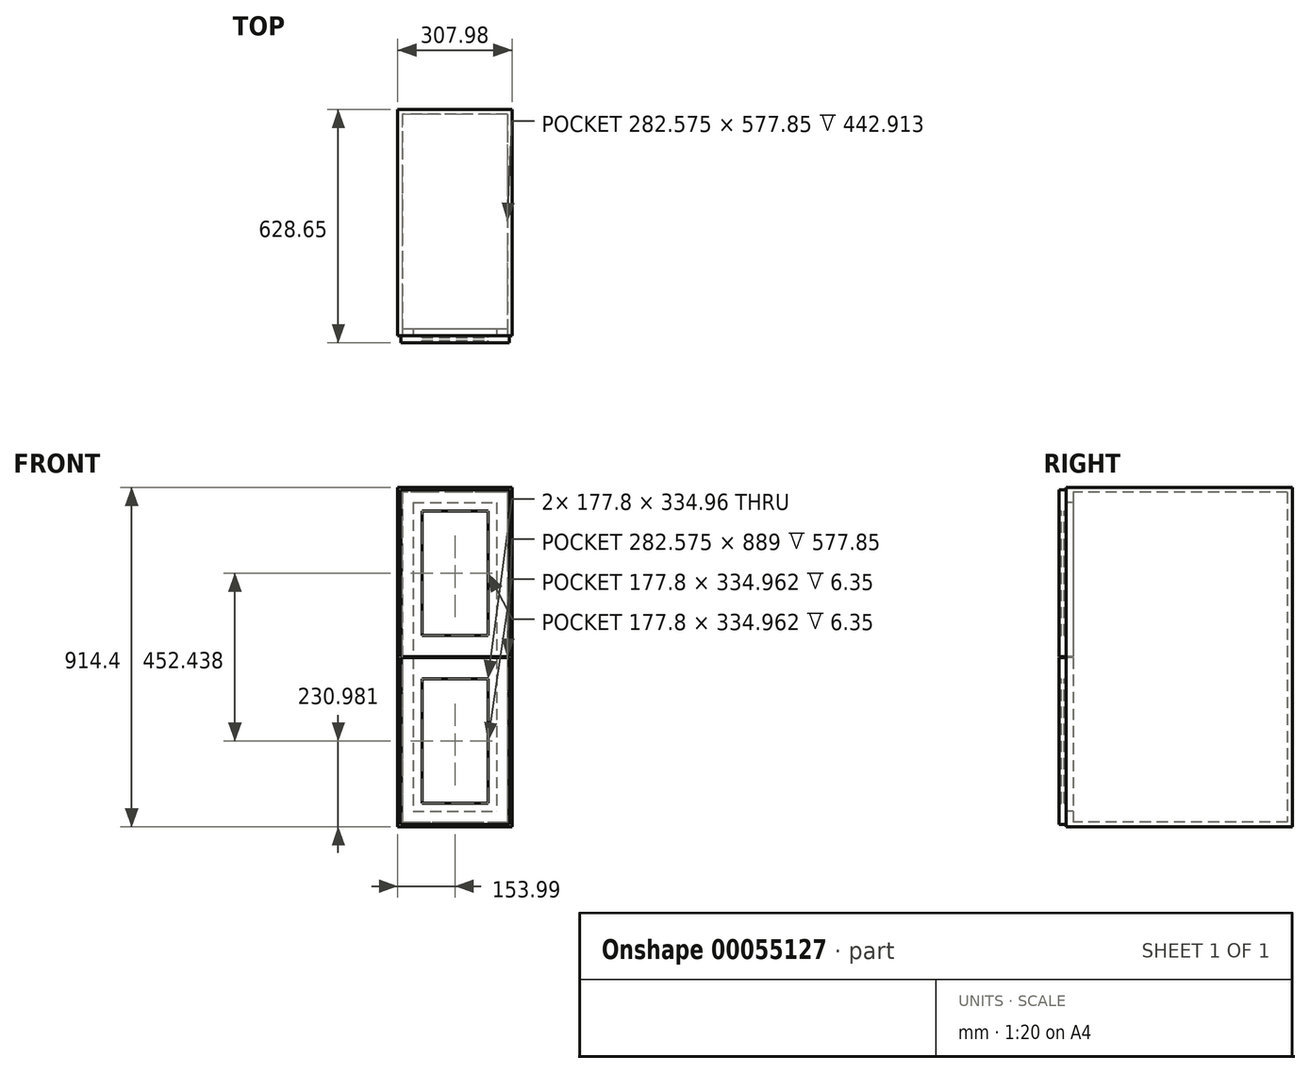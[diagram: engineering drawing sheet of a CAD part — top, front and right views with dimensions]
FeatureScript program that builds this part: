
annotation { "Feature Type Name" : "Feature", "Feature Type Description" : "" }
export const myFeature = defineFeature(function(context is Context, id is Id, definition is map)
    precondition{}
    {
        {
            var Q0;
            Q0=qCreatedBy(makeId("Top.planeOp"),FACE);
            var sketch = newSketch(context, id + "F0", { "sketchPlane" : qUnion([Q0])});
            skLineSegment(sketch, "E0.rect.bottom", {"start": v(153.99, 304.8) * mm, "end": v(-153.99, 304.8) * mm});
            skLineSegment(sketch, "E0.rect.top", {"start": v(153.99, -304.8) * mm, "end": v(-153.99, -304.8) * mm});
            skLineSegment(sketch, "E0.rect.left", {"start": v(153.99, 304.8) * mm, "end": v(153.99, -304.8) * mm});
            skLineSegment(sketch, "E0.rect.right", {"start": v(-153.99, 304.8) * mm, "end": v(-153.99, -304.8) * mm});
            skPoint(sketch, "E0.rect.middle", {"position": v(0, 0) * mm});
            skSolve(sketch);
        }
        {
            var Q0;
            Q0=qSketchRegion(id+"F0",true);
            extrude(context, id + "F1", {"entities" : qUnion([Q0]), "depth" : 914.4 * mm});
        }
        {
            var Q0;
            Q0=makeQuery(id+"F1.opExtrude","SWEPT_FACE",FACE,{"disambiguationData":[OSD([sQuery(id+"F0.wireOp",EDGE,"E0.rect.top")])]});
            shell(context, id + "F2", {"entities" : qUnion([Q0]), "thickness" : 12.7 * mm});
        }
        {
            var Q0;
            Q0=makeQuery(id+"F1.opExtrude","SWEPT_FACE",FACE,{"disambiguationData":[OSD([sQuery(id+"F0.wireOp",EDGE,"E0.rect.top")])]});
            var sketch = newSketch(context, id + "F3", { "sketchPlane" : qUnion([Q0])});
            skLineSegment(sketch, "E1", {"start": v(-153.99, 457.2) * mm, "end": v(153.99, 457.2) * mm, "construction": true});
            skLineSegment(sketch, "E2.rect.bottom", {"start": v(-153.99, 436.56) * mm, "end": v(153.99, 436.56) * mm});
            skLineSegment(sketch, "E2.rect.top", {"start": v(-153.99, 477.84) * mm, "end": v(153.99, 477.84) * mm});
            skLineSegment(sketch, "E2.rect.left", {"start": v(-153.99, 436.56) * mm, "end": v(-153.99, 477.84) * mm});
            skLineSegment(sketch, "E2.rect.right", {"start": v(153.99, 436.56) * mm, "end": v(153.99, 477.84) * mm});
            skPoint(sketch, "E2.rect.middle", {"position": v(0, 457.2) * mm});
            skLineSegment(sketch, "E3.bottom", {"start": v(-146.05, 6.35) * mm, "end": v(146.05, 6.35) * mm});
            skLineSegment(sketch, "E3.top", {"start": v(-146.05, 455.61) * mm, "end": v(146.05, 455.61) * mm});
            skLineSegment(sketch, "E3.left", {"start": v(-146.05, 6.35) * mm, "end": v(-146.05, 455.61) * mm});
            skLineSegment(sketch, "E3.right", {"start": v(146.05, 6.35) * mm, "end": v(146.05, 455.61) * mm});
            skLineSegment(sketch, "E4.rect.bottom", {"start": v(-112.71, 873.13) * mm, "end": v(112.71, 873.13) * mm});
            skLineSegment(sketch, "E4.rect.top", {"start": v(-112.71, 41.28) * mm, "end": v(112.71, 41.28) * mm});
            skLineSegment(sketch, "E4.rect.left", {"start": v(-112.71, 873.13) * mm, "end": v(-112.71, 41.28) * mm});
            skLineSegment(sketch, "E4.rect.right", {"start": v(112.71, 873.13) * mm, "end": v(112.71, 41.28) * mm});
            skLineSegment(sketch, "E5.bottom", {"start": v(-88.9, 63.5) * mm, "end": v(88.9, 63.5) * mm});
            skLineSegment(sketch, "E5.top", {"start": v(-88.9, 398.46) * mm, "end": v(88.9, 398.46) * mm});
            skLineSegment(sketch, "E5.left", {"start": v(-88.9, 63.5) * mm, "end": v(-88.9, 398.46) * mm});
            skLineSegment(sketch, "E5.right", {"start": v(88.9, 63.5) * mm, "end": v(88.9, 398.46) * mm});
            skLineSegment(sketch, "E6.bottom", {"start": v(-146.05, 458.79) * mm, "end": v(146.05, 458.79) * mm});
            skLineSegment(sketch, "E6.top", {"start": v(-146.05, 908.05) * mm, "end": v(146.05, 908.05) * mm});
            skLineSegment(sketch, "E6.left", {"start": v(-146.05, 458.79) * mm, "end": v(-146.05, 908.05) * mm});
            skLineSegment(sketch, "E6.right", {"start": v(146.05, 458.79) * mm, "end": v(146.05, 908.05) * mm});
            skLineSegment(sketch, "E7.bottom", {"start": v(-88.9, 515.94) * mm, "end": v(88.9, 515.94) * mm});
            skLineSegment(sketch, "E7.top", {"start": v(-88.9, 850.9) * mm, "end": v(88.9, 850.9) * mm});
            skLineSegment(sketch, "E7.left", {"start": v(-88.9, 515.94) * mm, "end": v(-88.9, 850.9) * mm});
            skLineSegment(sketch, "E7.right", {"start": v(88.9, 515.94) * mm, "end": v(88.9, 850.9) * mm});
            skSolve(sketch);
        }
        {
            var Q0;
            {var subQ1=sQuery(id+"F3.wireOp",EDGE,"E4.rect.bottom");Q0=makeQuery(id+"F3.imprint","IMPRINT",FACE,{"disambiguationData":[TD([[makeQuery(id+"F3.imprint","IMPRINT",EDGE,{"derivedFrom":subQ1}),1.0]])]});}
            var Q1;
            {var subQ0=sQuery(id+"F0.wireOp",EDGE,"E0.rect.top");var subQ1=makeQuery(id+"F1.opExtrude","CAP_EDGE",EDGE,{"disambiguationData":[OSD([subQ0])],"isStart":false});Q1=makeQuery(id+"F3.imprint","IMPRINT",FACE,{"disambiguationData":[TD([[makeQuery(id+"F3.imprint","IMPRINT",EDGE,{"derivedFrom":subQ1}),1.0]])]});}
            var Q2;
            {var subQ0=sQuery(id+"F3.wireOp",EDGE,"E4.rect.top");Q2=makeQuery(id+"F3.imprint","IMPRINT",FACE,{"disambiguationData":[TD([[makeQuery(id+"F3.imprint","IMPRINT",EDGE,{"derivedFrom":subQ0}),-1.0]])]});}
            var Q3;
            {var subQ1=sQuery(id+"F3.wireOp",EDGE,"E3.bottom");Q3=makeQuery(id+"F3.imprint","IMPRINT",FACE,{"disambiguationData":[TD([[makeQuery(id+"F3.imprint","IMPRINT",EDGE,{"derivedFrom":subQ1}),-1.0]])]});}
            var Q4;
            {var subQ0=sQuery(id+"F3.wireOp",EDGE,"E3.bottom");Q4=makeQuery(id+"F3.imprint","IMPRINT",FACE,{"disambiguationData":[TD([[makeQuery(id+"F3.imprint","IMPRINT",EDGE,{"derivedFrom":subQ0}),1.0]])]});}
            var Q5;
            {var subQ0=sQuery(id+"F3.wireOp",EDGE,"E4.rect.left");var subQ1=sQuery(id+"F3.wireOp",EDGE,"E2.rect.bottom");var subQ2=makeQuery(id+"F3.imprint","INTERSECT",VERTEX,{"derivedFrom":[subQ1,subQ0]});Q5=makeQuery(id+"F3.imprint","IMPRINT",FACE,{"disambiguationData":[TD([[makeQuery(id+"F3.imprint","IMPRINT",EDGE,{"disambiguationData":[TD([[subQ2,1.0]])],"derivedFrom":subQ0}),-1.0]])]});}
            var Q6;
            {var subQ0=sQuery(id+"F3.wireOp",EDGE,"E2.rect.left");Q6=makeQuery(id+"F3.imprint","IMPRINT",FACE,{"disambiguationData":[TD([[makeQuery(id+"F3.imprint","IMPRINT",EDGE,{"derivedFrom":subQ0}),1.0]])]});}
            var Q7;
            {var subQ0=sQuery(id+"F3.wireOp",EDGE,"E3.left");var subQ5=sQuery(id+"F3.wireOp",EDGE,"E3.top");var subQ6=makeQuery(id+"F3.imprint","INTERSECT",VERTEX,{"derivedFrom":[subQ5,subQ0]});Q7=makeQuery(id+"F3.imprint","IMPRINT",FACE,{"disambiguationData":[TD([[makeQuery(id+"F3.imprint","IMPRINT",EDGE,{"disambiguationData":[TD([[subQ6,1.0]])],"derivedFrom":subQ0}),-1.0]])]});}
            var Q8;
            {var subQ0=sQuery(id+"F3.wireOp",EDGE,"E4.rect.left");var subQ1=sQuery(id+"F3.wireOp",EDGE,"E2.rect.top");var subQ2=makeQuery(id+"F3.imprint","INTERSECT",VERTEX,{"derivedFrom":[subQ1,subQ0]});Q8=makeQuery(id+"F3.imprint","IMPRINT",FACE,{"disambiguationData":[TD([[makeQuery(id+"F3.imprint","IMPRINT",EDGE,{"disambiguationData":[TD([[subQ2,-1.0]])],"derivedFrom":subQ0}),-1.0]])]});}
            var Q9;
            {var subQ0=sQuery(id+"F3.wireOp",EDGE,"E4.rect.right");var subQ1=sQuery(id+"F3.wireOp",EDGE,"E2.rect.top");var subQ2=makeQuery(id+"F3.imprint","INTERSECT",VERTEX,{"derivedFrom":[subQ1,subQ0]});Q9=makeQuery(id+"F3.imprint","IMPRINT",FACE,{"disambiguationData":[TD([[makeQuery(id+"F3.imprint","IMPRINT",EDGE,{"disambiguationData":[TD([[subQ2,-1.0]])],"derivedFrom":subQ0}),1.0]])]});}
            var Q10;
            {var subQ0=sQuery(id+"F3.wireOp",EDGE,"E4.rect.right");var subQ1=sQuery(id+"F3.wireOp",EDGE,"E2.rect.bottom");var subQ2=makeQuery(id+"F3.imprint","INTERSECT",VERTEX,{"derivedFrom":[subQ1,subQ0]});Q10=makeQuery(id+"F3.imprint","IMPRINT",FACE,{"disambiguationData":[TD([[makeQuery(id+"F3.imprint","IMPRINT",EDGE,{"disambiguationData":[TD([[subQ2,1.0]])],"derivedFrom":subQ0}),1.0]])]});}
            var Q11;
            {var subQ7=sQuery(id+"F3.wireOp",EDGE,"E2.rect.right");Q11=makeQuery(id+"F3.imprint","IMPRINT",FACE,{"disambiguationData":[TD([[makeQuery(id+"F3.imprint","IMPRINT",EDGE,{"derivedFrom":subQ7}),-1.0]])]});}
            var Q12;
            {var subQ0=sQuery(id+"F3.wireOp",EDGE,"E3.right");var subQ5=sQuery(id+"F3.wireOp",EDGE,"E3.top");var subQ6=makeQuery(id+"F3.imprint","INTERSECT",VERTEX,{"derivedFrom":[subQ5,subQ0]});Q12=makeQuery(id+"F3.imprint","IMPRINT",FACE,{"disambiguationData":[TD([[makeQuery(id+"F3.imprint","IMPRINT",EDGE,{"disambiguationData":[TD([[subQ6,1.0]])],"derivedFrom":subQ0}),1.0]])]});}
            extrude(context, id + "F4", {"entities" : qUnion([Q0, Q1, Q2, Q3, Q4, Q5, Q6, Q7, Q8, Q9, Q10, Q11, Q12]), "operationType" : NewBodyOperationType.ADD, "oppositeDirection" : true, "depth" : 19.05 * mm});
        }
        {
            var Q0;
            {var subQ0=sQuery(id+"F3.wireOp",EDGE,"E4.rect.top");Q0=makeQuery(id+"F3.imprint","IMPRINT",FACE,{"disambiguationData":[TD([[makeQuery(id+"F3.imprint","IMPRINT",EDGE,{"derivedFrom":subQ0}),-1.0]])]});}
            var Q1;
            {var subQ0=sQuery(id+"F3.wireOp",EDGE,"E3.bottom");Q1=makeQuery(id+"F3.imprint","IMPRINT",FACE,{"disambiguationData":[TD([[makeQuery(id+"F3.imprint","IMPRINT",EDGE,{"derivedFrom":subQ0}),1.0]])]});}
            var Q2;
            {var subQ1=sQuery(id+"F3.wireOp",EDGE,"E4.rect.top");Q2=makeQuery(id+"F3.imprint","IMPRINT",FACE,{"disambiguationData":[TD([[makeQuery(id+"F3.imprint","IMPRINT",EDGE,{"derivedFrom":subQ1}),1.0]])]});}
            var Q3;
            {var subQ0=sQuery(id+"F3.wireOp",EDGE,"E4.rect.left");var subQ1=sQuery(id+"F3.wireOp",EDGE,"E2.rect.bottom");var subQ2=makeQuery(id+"F3.imprint","INTERSECT",VERTEX,{"derivedFrom":[subQ1,subQ0]});Q3=makeQuery(id+"F3.imprint","IMPRINT",FACE,{"disambiguationData":[TD([[makeQuery(id+"F3.imprint","IMPRINT",EDGE,{"disambiguationData":[TD([[subQ2,-1.0]])],"derivedFrom":subQ1}),1.0]])]});}
            var Q4;
            {var subQ0=sQuery(id+"F3.wireOp",EDGE,"E4.rect.left");var subQ1=sQuery(id+"F3.wireOp",EDGE,"E2.rect.bottom");var subQ2=makeQuery(id+"F3.imprint","INTERSECT",VERTEX,{"derivedFrom":[subQ1,subQ0]});Q4=makeQuery(id+"F3.imprint","IMPRINT",FACE,{"disambiguationData":[TD([[makeQuery(id+"F3.imprint","IMPRINT",EDGE,{"disambiguationData":[TD([[subQ2,1.0]])],"derivedFrom":subQ0}),-1.0]])]});}
            var Q5;
            {var subQ0=sQuery(id+"F3.wireOp",EDGE,"E4.rect.right");var subQ1=sQuery(id+"F3.wireOp",EDGE,"E2.rect.bottom");var subQ2=makeQuery(id+"F3.imprint","INTERSECT",VERTEX,{"derivedFrom":[subQ1,subQ0]});Q5=makeQuery(id+"F3.imprint","IMPRINT",FACE,{"disambiguationData":[TD([[makeQuery(id+"F3.imprint","IMPRINT",EDGE,{"disambiguationData":[TD([[subQ2,1.0]])],"derivedFrom":subQ0}),1.0]])]});}
            var Q6;
            {var subQ0=sQuery(id+"F3.wireOp",EDGE,"E3.right");var subQ5=sQuery(id+"F3.wireOp",EDGE,"E3.top");var subQ6=makeQuery(id+"F3.imprint","INTERSECT",VERTEX,{"derivedFrom":[subQ5,subQ0]});Q6=makeQuery(id+"F3.imprint","IMPRINT",FACE,{"disambiguationData":[TD([[makeQuery(id+"F3.imprint","IMPRINT",EDGE,{"disambiguationData":[TD([[subQ6,1.0]])],"derivedFrom":subQ0}),1.0]])]});}
            var Q7;
            {var subQ0=sQuery(id+"F3.wireOp",EDGE,"E3.left");var subQ5=sQuery(id+"F3.wireOp",EDGE,"E3.top");var subQ6=makeQuery(id+"F3.imprint","INTERSECT",VERTEX,{"derivedFrom":[subQ5,subQ0]});Q7=makeQuery(id+"F3.imprint","IMPRINT",FACE,{"disambiguationData":[TD([[makeQuery(id+"F3.imprint","IMPRINT",EDGE,{"disambiguationData":[TD([[subQ6,1.0]])],"derivedFrom":subQ0}),-1.0]])]});}
            var Q8;
            {var subQ0=sQuery(id+"F3.wireOp",EDGE,"E4.rect.bottom");Q8=makeQuery(id+"F3.imprint","IMPRINT",FACE,{"disambiguationData":[TD([[makeQuery(id+"F3.imprint","IMPRINT",EDGE,{"derivedFrom":subQ0}),1.0]])]});}
            var Q9;
            {var subQ1=sQuery(id+"F3.wireOp",EDGE,"E4.rect.bottom");Q9=makeQuery(id+"F3.imprint","IMPRINT",FACE,{"disambiguationData":[TD([[makeQuery(id+"F3.imprint","IMPRINT",EDGE,{"derivedFrom":subQ1}),-1.0]])]});}
            var Q10;
            {var subQ0=sQuery(id+"F3.wireOp",EDGE,"E4.rect.left");var subQ1=sQuery(id+"F3.wireOp",EDGE,"E2.rect.top");var subQ2=makeQuery(id+"F3.imprint","INTERSECT",VERTEX,{"derivedFrom":[subQ1,subQ0]});Q10=makeQuery(id+"F3.imprint","IMPRINT",FACE,{"disambiguationData":[TD([[makeQuery(id+"F3.imprint","IMPRINT",EDGE,{"disambiguationData":[TD([[subQ2,-1.0]])],"derivedFrom":subQ0}),-1.0]])]});}
            var Q11;
            {var subQ0=sQuery(id+"F3.wireOp",EDGE,"E4.rect.left");var subQ1=sQuery(id+"F3.wireOp",EDGE,"E2.rect.top");var subQ2=makeQuery(id+"F3.imprint","INTERSECT",VERTEX,{"derivedFrom":[subQ1,subQ0]});Q11=makeQuery(id+"F3.imprint","IMPRINT",FACE,{"disambiguationData":[TD([[makeQuery(id+"F3.imprint","IMPRINT",EDGE,{"disambiguationData":[TD([[subQ2,-1.0]])],"derivedFrom":subQ1}),-1.0]])]});}
            var Q12;
            {var subQ0=sQuery(id+"F3.wireOp",EDGE,"E4.rect.right");var subQ1=sQuery(id+"F3.wireOp",EDGE,"E2.rect.top");var subQ2=makeQuery(id+"F3.imprint","INTERSECT",VERTEX,{"derivedFrom":[subQ1,subQ0]});Q12=makeQuery(id+"F3.imprint","IMPRINT",FACE,{"disambiguationData":[TD([[makeQuery(id+"F3.imprint","IMPRINT",EDGE,{"disambiguationData":[TD([[subQ2,-1.0]])],"derivedFrom":subQ0}),1.0]])]});}
            var Q13;
            {var subQ0=sQuery(id+"F3.wireOp",EDGE,"E6.right");var subQ5=sQuery(id+"F3.wireOp",EDGE,"E6.bottom");var subQ6=makeQuery(id+"F3.imprint","INTERSECT",VERTEX,{"derivedFrom":[subQ5,subQ0]});Q13=makeQuery(id+"F3.imprint","IMPRINT",FACE,{"disambiguationData":[TD([[makeQuery(id+"F3.imprint","IMPRINT",EDGE,{"disambiguationData":[TD([[subQ6,-1.0]])],"derivedFrom":subQ0}),1.0]])]});}
            var Q14;
            {var subQ1=sQuery(id+"F3.wireOp",EDGE,"E6.top");Q14=makeQuery(id+"F3.imprint","IMPRINT",FACE,{"disambiguationData":[TD([[makeQuery(id+"F3.imprint","IMPRINT",EDGE,{"derivedFrom":subQ1}),-1.0]])]});}
            var Q15;
            {var subQ0=sQuery(id+"F3.wireOp",EDGE,"E6.left");var subQ5=sQuery(id+"F3.wireOp",EDGE,"E6.bottom");var subQ6=makeQuery(id+"F3.imprint","INTERSECT",VERTEX,{"derivedFrom":[subQ5,subQ0]});Q15=makeQuery(id+"F3.imprint","IMPRINT",FACE,{"disambiguationData":[TD([[makeQuery(id+"F3.imprint","IMPRINT",EDGE,{"disambiguationData":[TD([[subQ6,-1.0]])],"derivedFrom":subQ0}),-1.0]])]});}
            extrude(context, id + "F5", {"entities" : qUnion([Q0, Q1, Q2, Q3, Q4, Q5, Q6, Q7, Q8, Q9, Q10, Q11, Q12, Q13, Q14, Q15]), "operationType" : NewBodyOperationType.ADD, "depth" : 19.05 * mm});
        }
        {
            var Q0;
            Q0=makeQuery(id+"F5.opExtrude","SWEPT_FACE",FACE,{"disambiguationData":[OSD([sQuery(id+"F3.wireOp",EDGE,"E5.right")])]});
            var sketch = newSketch(context, id + "F6", { "sketchPlane" : qUnion([Q0])});
            skLineSegment(sketch, "E8.bottom", {"start": v(309.56, 63.5) * mm, "end": v(317.5, 63.5) * mm});
            skLineSegment(sketch, "E8.top", {"start": v(309.56, 398.46) * mm, "end": v(317.5, 398.46) * mm});
            skLineSegment(sketch, "E8.left", {"start": v(309.56, 63.5) * mm, "end": v(309.56, 398.46) * mm});
            skLineSegment(sketch, "E8.right", {"start": v(317.5, 63.5) * mm, "end": v(317.5, 398.46) * mm});
            skLineSegment(sketch, "E9.bottom", {"start": v(309.56, 515.94) * mm, "end": v(317.5, 515.94) * mm});
            skLineSegment(sketch, "E9.top", {"start": v(309.56, 850.9) * mm, "end": v(317.5, 850.9) * mm});
            skLineSegment(sketch, "E9.left", {"start": v(309.56, 515.94) * mm, "end": v(309.56, 850.9) * mm});
            skLineSegment(sketch, "E9.right", {"start": v(317.5, 515.94) * mm, "end": v(317.5, 850.9) * mm});
            skSolve(sketch);
        }
        {
            var Q0;
            Q0 = qSketchRegion(id + "F6", true);
            extrude(context, id + "F7", {"entities" : qUnion([Q0]), "operationType" : NewBodyOperationType.ADD, "endBound" : BoundingType.UP_TO_NEXT, "depth" : 25.4 * mm});
        }
    });
